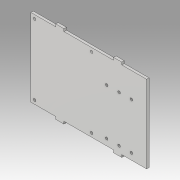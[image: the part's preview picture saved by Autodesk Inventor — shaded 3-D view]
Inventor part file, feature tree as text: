
AUTODESK INVENTOR PART (.ipt)
format: ipt  version: 2019.3 (Build 233278000, 278)  size: 140,800 bytes
history: native  units: mm
features: extrude x2, sketch x2
ambient origin geometry x8: Origin, YZ Plane, XZ Plane, XY Plane, X Axis, Y Axis, Z Axis, Center Point
bodies: Solid1 (feature_tree)
feature tree (4):
  extrude  "Extrusion1"  Depth=85.0mm
  extrude  "Extrusion2"  Depth=94.0mm
  sketch  "Sketch1"  dims[d0=3.1mm d1=85.0mm]
  sketch  "Sketch2"  dims[d2=69.0mm d3=94.0mm d4=4.5mm d5=4.5mm d6=4.5mm d7=140.0mm d12=30.0mm d13=30.0mm d14=3.0mm d15=0.0mm d16=10.0mm d17=3.0mm d18=10.0mm d19=3.0mm d20=56.0mm d21=15.0mm d22=15.0mm d23=7.75mm d24=33.25mm d25=33.25mm d26=3.0mm d27=0.0mm]
